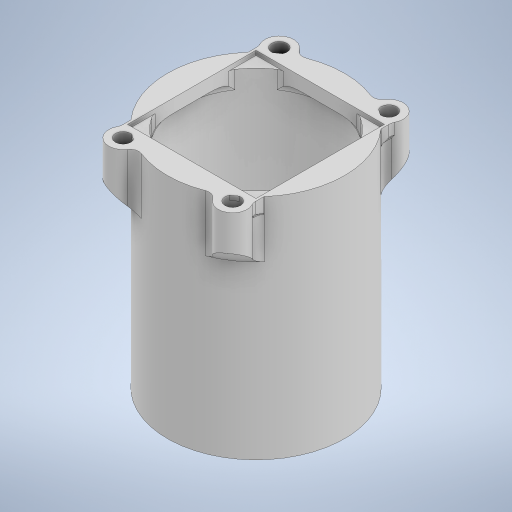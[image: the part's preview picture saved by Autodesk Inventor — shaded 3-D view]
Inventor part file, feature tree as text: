
AUTODESK INVENTOR PART (.ipt)
format: ipt  version: 2024 (Build 280153000, 153)  size: 567,808 bytes
history: native  units: in
note: dims shown in document units (in); Inventor stores cm internally (conversion verified against a paired STEP export)
features: extrude x9, projected_geometry x6, sketch x5, fillet x4, chamfer x1
ambient origin geometry x8: Origin, YZ Plane, XZ Plane, XY Plane, X Axis, Y Axis, Z Axis, Center Point
bodies: Solid1 (feature_tree)
feature tree (25):
  extrude  "Extrusion1"  Depth=1.5748in
  extrude  "Extrusion2"  Depth=0.9843in
  extrude  "Extrusion3"  Depth=0.1181in
  sketch  "Sketch4"  dims[d8=1.7106in d9=0.0in d10=0.1378in]
  extrude  "Extrusion4"  Depth=0.1378in
  extrude  "Extrusion5"  Depth=0.0787in
  extrude  "Extrusion6"  Depth=0.0787in
  extrude  "Extrusion7"  Depth=0.0787in
  extrude  "Extrusion8"  Depth=0.0787in
  fillet  "Fillet1"  Radius=0.2559in
  extrude  "Extrusion9"  Depth=0.0787in
  chamfer  "Chamfer1"  Distance=0.5906in
  fillet  "Fillet4"  Radius=0.5906in
  fillet  "Fillet5"  Radius=0.2362in
  fillet  "Fillet6"  Radius=0.2362in
  sketch  "Sketch1"  dims[d0=0.8386in d1=1.5748in]
  sketch  "Sketch2"  dims[d2=0.1181in d3=0.0in d4=0.9843in]
  sketch  "Sketch3"  dims[d5=0.1575in d6=0.0in d7=0.1181in]
  projected_geometry  "Projected Loop1"
  projected_geometry  "Projected Loop2"
  sketch  "Sketch5"  dims[d14=1.3878in d15=0.9744in d17=0.9744in d18=0.4872in d19=0.6939in d20=0.2559in d21=1.1811in d22=0.5906in d23=0.5906in d25=0.2362in d26=0.0in d27=0.2362in d28=0.0in d29=0.0197in d30=1.3878in d31=0.0787in d32=0.0in d33=0.0394in d34=0.0in d35=0.0394in d36=0.0in d37=0.0787in d39=0.0394in d40=0.0in d42=0.187in d43=0.0787in d44=45.0deg d45=0.0197in d46=0.0787in d47=0.0787in d41=0.0in]
  projected_geometry  "Projected Loop3"
  projected_geometry  "Projected Loop4"
  projected_geometry  "Projected Loop5"
  projected_geometry  "Projected Loop6"
